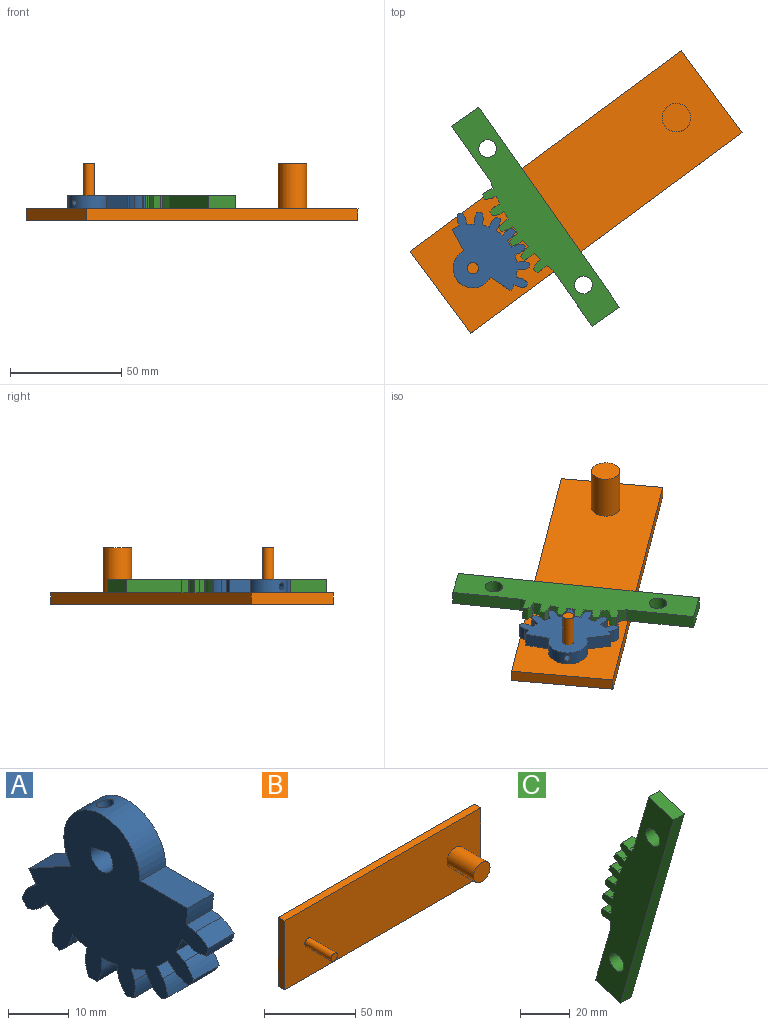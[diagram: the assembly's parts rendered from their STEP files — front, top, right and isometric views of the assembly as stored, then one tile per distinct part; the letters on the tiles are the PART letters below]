
ASSEMBLY  parts=3 mates=2
PART A: 51 faces, bbox 6x43.4x34.3 mm
  f0: plane 43.38x34.23mm, normal (1,0,0), area 767.3mm2, adj f2,f3,f4,f5,f6,f7,f8,f9
  f1: plane 43.38x34.23mm, normal (-1,0,0), area 767.3mm2, adj f2,f3,f4,f5,f6,f7,f8,f9
  f2: cylinder r=19.92mm len=5.99mm, axis (-1,0,0), area 20.8mm2, adj f0,f1,f7,f9
  f3: plane 5.99x2.18mm, normal (0,-0.17,0.98), area 13.3mm2, adj f0,f1,f4,f44
  f4: extruded ~5.99x2.97mm, area 21mm2, adj f0,f1,f3,f5
  f5: cylinder r=25.4mm len=5.99mm, axis (-1,0,0), area 11.3mm2, adj f0,f1,f4,f6
  f6: extruded ~5.99x3.48mm, area 21mm2, adj f0,f1,f5,f7
  f7: plane 5.99x2.08mm, normal (0,0.34,-0.94), area 13.3mm2, adj f0,f1,f2,f6
  f8: cylinder r=19.92mm len=5.99mm, axis (-1,0,0), area 20.8mm2, adj f0,f1,f13,f15
  f9: plane 5.99x1.91mm, normal (0,-0.5,0.87), area 13.3mm2, adj f0,f1,f2,f10
  f10: extruded ~5.99x2.72mm, area 21mm2, adj f0,f1,f9,f11
  f11: cylinder r=25.4mm len=5.99mm, axis (-1,0,0), area 11.3mm2, adj f0,f1,f10,f12
  f12: extruded ~5.99x3.3mm, area 21mm2, adj f0,f1,f11,f13
  f13: plane 5.99x1.69mm, normal (0,0.64,-0.77), area 13.3mm2, adj f0,f1,f8,f12
  f14: cylinder r=19.92mm len=5.99mm, axis (-1,0,0), area 20.8mm2, adj f0,f1,f19,f21
  f15: plane 5.99x1.69mm, normal (0,-0.77,0.64), area 13.3mm2, adj f0,f1,f8,f16
  f16: extruded ~5.99x3.3mm, area 21mm2, adj f0,f1,f15,f17
  f17: cylinder r=25.4mm len=5.99mm, axis (-1,0,0), area 11.3mm2, adj f0,f1,f16,f18
  f18: extruded ~5.99x2.72mm, area 21mm2, adj f0,f1,f17,f19
  f19: plane 5.99x1.91mm, normal (0,0.87,-0.5), area 13.3mm2, adj f0,f1,f14,f18
  f20: cylinder r=19.92mm len=5.99mm, axis (-1,0,0), area 20.8mm2, adj f0,f1,f25,f27
  f21: plane 5.99x2.08mm, normal (0,-0.94,0.34), area 13.3mm2, adj f0,f1,f14,f22
  f22: extruded ~5.99x3.48mm, area 21mm2, adj f0,f1,f21,f23
  f23: cylinder r=25.4mm len=5.99mm, axis (-1,0,0), area 11.3mm2, adj f0,f1,f22,f24
  f24: extruded ~5.99x2.97mm, area 21mm2, adj f0,f1,f23,f25
  f25: plane 5.99x2.18mm, normal (0,0.98,-0.17), area 13.3mm2, adj f0,f1,f20,f24
  f26: cylinder r=19.92mm len=5.99mm, axis (-1,0,0), area 20.8mm2, adj f0,f1,f31,f33
  f27: plane 5.99x2.21mm, normal (0,-1,0), area 13.3mm2, adj f0,f1,f20,f28
  f28: extruded ~5.99x3.24mm, area 21mm2, adj f0,f1,f27,f29
  f29: cylinder r=25.4mm len=5.99mm, axis (-1,0,0), area 11.3mm2, adj f0,f1,f28,f30
  f30: extruded ~5.99x3.41mm, area 21mm2, adj f0,f1,f29,f31
  f31: plane 5.99x2.18mm, normal (0,0.98,0.17), area 13.3mm2, adj f0,f1,f26,f30
  f32: cylinder r=19.92mm len=5.99mm, axis (-1,0,0), area 20.8mm2, adj f0,f1,f37,f39
  f33: plane 5.99x2.08mm, normal (0,-0.94,-0.34), area 13.3mm2, adj f0,f1,f26,f34
  f34: extruded ~5.99x2.6mm, area 21mm2, adj f0,f1,f33,f35
  f35: cylinder r=25.4mm len=5.99mm, axis (-1,0,0), area 11.3mm2, adj f0,f1,f34,f36
  f36: extruded ~5.99x3.44mm, area 21mm2, adj f0,f1,f35,f37
  f37: plane 5.99x1.91mm, normal (0,0.87,0.5), area 13.3mm2, adj f0,f1,f32,f36
  f38: cylinder r=19.92mm len=5.99mm, axis (-1,0,0), area 17.8mm2, adj f0,f1,f43,f48
  f39: plane 5.99x1.69mm, normal (0,-0.77,-0.64), area 13.3mm2, adj f0,f1,f32,f40
  f40: extruded ~5.99x3.06mm, area 21mm2, adj f0,f1,f39,f41
  f41: cylinder r=25.4mm len=5.99mm, axis (-1,0,0), area 11.3mm2, adj f0,f1,f40,f42
  f42: extruded ~5.99x3.06mm, area 21mm2, adj f0,f1,f41,f43
  f43: plane 5.99x1.69mm, normal (0,0.64,0.77), area 13.3mm2, adj f0,f1,f38,f42
  f44: cylinder r=19.92mm len=5.99mm, axis (-1,0,0), area 20.8mm2, adj f0,f1,f3,f50
  f45: cylinder r=2.54mm len=5.99mm, axis (-1,0,0), area 69.5mm2, adj f0,f1,f46
  f46: plane 5.99x3.71mm, normal (0,-0.26,-0.97), area 16mm2, adj f0,f1,f45,f47
  f47: cylinder r=1.5mm len=7.73mm, axis (0,-0.26,-0.97), area 67.2mm2, adj f46,f49
  f48: plane 9.71x5.99mm, normal (0,0.48,0.88), area 66.5mm2, adj f0,f1,f38,f49
  f49: cylinder r=8.86mm len=17.72mm, axis (1,0,0), area 192.1mm2, adj f0,f1,f47,f48,f50
  f50: plane 11.06x5.99mm, normal (0,0,1), area 66.3mm2, adj f0,f1,f44,f49
PART B: 10 faces, bbox 151.8x25.4x46.2 mm
  f0: plane 151.83x5.08mm, normal (0,0,-1), area 771.3mm2, adj f1,f3,f4,f5
  f1: plane 46.15x5.08mm, normal (1,0,0), area 234.5mm2, adj f0,f2,f4,f5
  f2: plane 151.83x5.08mm, normal (0,0,1), area 771.3mm2, adj f1,f3,f4,f5
  f3: plane 46.15x5.08mm, normal (-1,0,0), area 234.5mm2, adj f0,f2,f4,f5
  f4: plane 151.83x46.15mm, normal (0,-1,0), area 6857.3mm2, adj f0,f1,f2,f3,f6,f8
  f5: plane 151.83x46.15mm, normal (0,1,0), area 7007.2mm2, adj f0,f1,f2,f3
  f6: cylinder r=2.54mm len=20.32mm, axis (0,1,0), area 324.3mm2, adj f4,f7
  f7: plane 5.08x5.08mm, normal (0,-1,0), area 20.3mm2, adj f6
  f8: cylinder r=6.42mm len=20.32mm, axis (0,1,0), area 820.1mm2, adj f4,f9
  f9: plane 12.85x12.85mm, normal (0,-1,0), area 129.6mm2, adj f8
PART C: 46 faces, bbox 6x44.7x109.9 mm
  f0: cylinder r=88.5mm len=5.99mm, axis (-1,0,0), area 18.5mm2, adj f1,f2,f38,f41
  f1: plane 109.88x44.74mm, normal (1,0,0), area 1776mm2, adj f0,f3,f4,f5,f6,f7,f8,f9
  f2: plane 109.88x44.74mm, normal (-1,0,0), area 1776mm2, adj f0,f3,f4,f5,f6,f7,f8,f9
  f3: cylinder r=88.5mm len=5.99mm, axis (-1,0,0), area 23.1mm2, adj f1,f2,f5,f43
  f4: cylinder r=88.5mm len=5.99mm, axis (-1,0,0), area 23.1mm2, adj f1,f2,f9,f11
  f5: plane 5.99x1.41mm, normal (0,0.04,-1), area 8.4mm2, adj f1,f2,f3,f6
  f6: extruded ~5.99x4.03mm, area 25mm2, adj f1,f2,f5,f7
  f7: cylinder r=93.98mm len=5.99mm, axis (-1,0,0), area 14.5mm2, adj f1,f2,f6,f8
  f8: extruded ~5.99x4.13mm, area 25mm2, adj f1,f2,f7,f9
  f9: plane 5.99x1.4mm, normal (0,-0.09,1), area 8.4mm2, adj f1,f2,f4,f8
  f10: cylinder r=88.5mm len=5.99mm, axis (-1,0,0), area 23.1mm2, adj f1,f2,f15,f17
  f11: plane 5.99x1.4mm, normal (0,0.13,-0.99), area 8.4mm2, adj f1,f2,f4,f12
  f12: extruded ~5.99x3.92mm, area 25mm2, adj f1,f2,f11,f13
  f13: cylinder r=93.98mm len=5.99mm, axis (-1,0,0), area 14.5mm2, adj f1,f2,f12,f14
  f14: extruded ~5.99x4.15mm, area 25mm2, adj f1,f2,f13,f15
  f15: plane 5.99x1.39mm, normal (0,-0.17,0.98), area 8.4mm2, adj f1,f2,f10,f14
  f16: cylinder r=88.5mm len=5.99mm, axis (-1,0,0), area 23.1mm2, adj f1,f2,f21,f23
  f17: plane 5.99x1.37mm, normal (0,0.22,-0.98), area 8.4mm2, adj f1,f2,f10,f18
  f18: extruded ~5.99x3.79mm, area 25mm2, adj f1,f2,f17,f19
  f19: cylinder r=93.98mm len=5.99mm, axis (-1,0,0), area 14.5mm2, adj f1,f2,f18,f20
  f20: extruded ~5.99x4.15mm, area 25mm2, adj f1,f2,f19,f21
  f21: plane 5.99x1.36mm, normal (0,-0.26,0.97), area 8.4mm2, adj f1,f2,f16,f20
  f22: cylinder r=88.5mm len=5.99mm, axis (-1,0,0), area 23.1mm2, adj f1,f2,f27,f29
  f23: plane 5.99x1.34mm, normal (0,0.3,-0.95), area 8.4mm2, adj f1,f2,f16,f24
  f24: extruded ~5.99x3.63mm, area 25mm2, adj f1,f2,f23,f25
  f25: cylinder r=93.98mm len=5.99mm, axis (-1,0,0), area 14.5mm2, adj f1,f2,f24,f26
  f26: extruded ~5.99x4.11mm, area 25mm2, adj f1,f2,f25,f27
  f27: plane 5.99x1.32mm, normal (0,-0.34,0.94), area 8.4mm2, adj f1,f2,f22,f26
  f28: cylinder r=88.5mm len=5.99mm, axis (-1,0,0), area 23.1mm2, adj f1,f2,f33,f34
  f29: plane 5.99x1.3mm, normal (0,0.38,-0.92), area 8.4mm2, adj f1,f2,f22,f30
  f30: extruded ~5.99x3.44mm, area 25mm2, adj f1,f2,f29,f31
  f31: cylinder r=93.98mm len=5.99mm, axis (-1,0,0), area 14.5mm2, adj f1,f2,f30,f32
  f32: extruded ~5.99x4.04mm, area 25mm2, adj f1,f2,f31,f33
  f33: plane 5.99x1.28mm, normal (0,-0.42,0.91), area 8.4mm2, adj f1,f2,f28,f32
  f34: plane 5.99x1.25mm, normal (0,0.46,-0.89), area 8.4mm2, adj f1,f2,f28,f35
  f35: extruded ~5.99x3.22mm, area 25mm2, adj f1,f2,f34,f36
  f36: cylinder r=93.98mm len=5.99mm, axis (-1,0,0), area 14.5mm2, adj f1,f2,f35,f37
  f37: extruded ~5.99x3.94mm, area 25mm2, adj f1,f2,f36,f38
  f38: plane 5.99x1.22mm, normal (0,-0.5,0.87), area 8.4mm2, adj f0,f1,f2,f37
  f39: plane 14.42x5.99mm, normal (0,-0.28,0.96), area 89.9mm2, adj f1,f2,f40,f41
  f40: plane 105.74x30.32mm, normal (0,-0.96,-0.28), area 659.4mm2, adj f1,f2,f39,f45
  f41: plane 29.42x8.44mm, normal (0,0.96,0.28), area 183.5mm2, adj f0,f1,f2,f39
  f42: cylinder r=4mm len=8mm, axis (1,0,0), area 150.7mm2, adj f1,f2
  f43: plane 29.42x8.44mm, normal (0,0.96,0.28), area 183.5mm2, adj f1,f2,f3,f45
  f44: cylinder r=4mm len=8mm, axis (1,0,0), area 150.7mm2, adj f1,f2
  f45: plane 14.42x5.99mm, normal (0,0.28,-0.96), area 89.9mm2, adj f1,f2,f40,f43
PLACE A rot(axis=(0.7,0.17,-0.7),160.2deg) t=(30.4,9.88,130.03)mm
PLACE B rot(axis=(-0.91,-0.3,0.3),95.6deg) t=(76.84,44.24,118.95)mm fixed
PLACE C rot(axis=(-0.69,0.24,0.69),152.8deg) t=(122.08,77.71,130.03)mm
MATE revolute B.f6 <-> A.f2  axis (0,0,1) through (30.4,9.88,124.03)mm
MATE revolute C.f0 <-> B.f8  axis (0,0,1) through (122.08,77.71,124.03)mm
